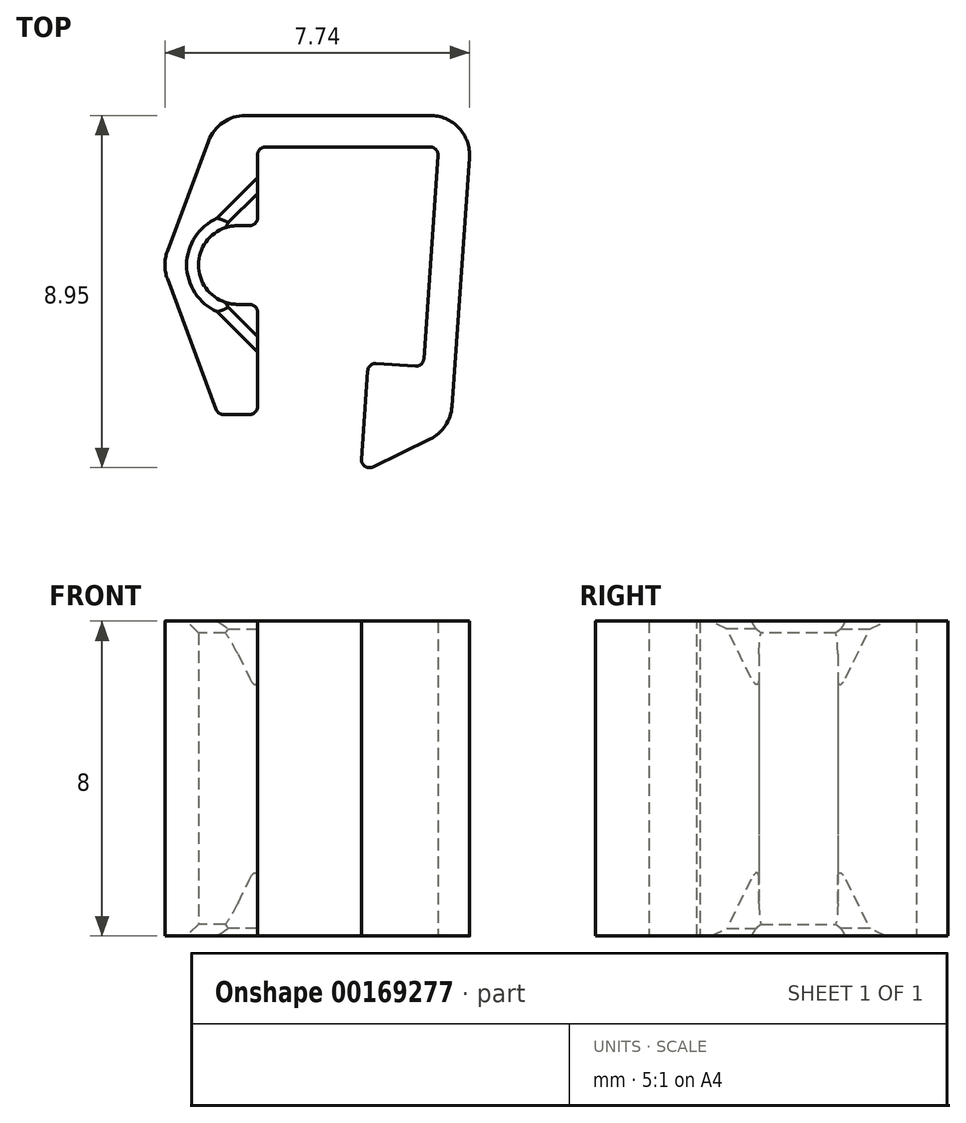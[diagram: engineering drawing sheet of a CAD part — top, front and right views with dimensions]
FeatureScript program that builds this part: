
annotation { "Feature Type Name" : "Feature", "Feature Type Description" : "" }
export const myFeature = defineFeature(function(context is Context, id is Id, definition is map)
    precondition{}
    {
        {
            var Q0;
            Q0=qCreatedBy(makeId("Top.planeOp"),FACE);
            var sketch = newSketch(context, id + "F0", { "sketchPlane" : qUnion([Q0])});
            skLineSegment(sketch, "E0", {"start": v(0, 0) * mm, "end": v(-0.4, -5.59) * mm});
            skLineSegment(sketch, "E1", {"start": v(-0.4, -5.59) * mm, "end": v(-1.79, -5.49) * mm});
            skLineSegment(sketch, "E2", {"start": v(-1.79, -5.49) * mm, "end": v(-1.98, -8.28) * mm});
            skLineSegment(sketch, "E3", {"start": v(-1.98, -8.28) * mm, "end": v(0.3, -7.17) * mm});
            skLineSegment(sketch, "E4", {"start": v(0.3, -7.17) * mm, "end": v(0.86, 0.8) * mm});
            skLineSegment(sketch, "E5", {"start": v(0.86, 0.8) * mm, "end": v(-5.6, 0.8) * mm});
            skLineSegment(sketch, "E6", {"start": v(-5.1, -4) * mm, "end": v(-4.6, -4) * mm});
            skLineSegment(sketch, "E7", {"start": v(-4.6, -4) * mm, "end": v(-4.6, -6.8) * mm});
            skLineSegment(sketch, "E8", {"start": v(-7.02, -3) * mm, "end": v(-5.6, -6.8) * mm});
            skLineSegment(sketch, "E9", {"start": v(-5.6, -6.8) * mm, "end": v(-4.6, -6.8) * mm});
            skLineSegment(sketch, "E10", {"start": v(-4.6, -2) * mm, "end": v(-5.1, -2) * mm});
            skLineSegment(sketch, "E11", {"start": v(0, 0) * mm, "end": v(-4.6, 0) * mm});
            skLineSegment(sketch, "E12", {"start": v(-4.6, 0) * mm, "end": v(-4.6, -2) * mm});
            skArc(sketch, "E13", {"start": v(-5.1, -2) * mm, "mid": v(-6.1, -3) * mm, "end": v(-5.1, -4) * mm});
            skLineSegment(sketch, "E14", {"start": v(-7.02, -3) * mm, "end": v(-5.6, 0.8) * mm});
            skLineSegment(sketch, "E15", {"start": v(-5.6, -6.8) * mm, "end": v(-5.6, 0.8) * mm, "construction": true});
            skLineSegment(sketch, "E16", {"start": v(-5.1, -3) * mm, "end": v(-6.04, -2.65) * mm, "construction": true});
            skLineSegment(sketch, "E17", {"start": v(-6.04, -2.65) * mm, "end": v(-6.79, -2.37) * mm, "construction": true});
            skLineSegment(sketch, "E18", {"start": v(0, 0) * mm, "end": v(0, 0.8) * mm, "construction": true});
            skLineSegment(sketch, "E19", {"start": v(0.8, -0.06) * mm, "end": v(0, 0) * mm, "construction": true});
            skSolve(sketch);
        }
        {
            var Q0;
            Q0 = qSketchRegion(id + "F0", true);
            extrude(context, id + "F1", {"entities" : qUnion([Q0]), "depth" : 4 * mm});
        }
        {
            var Q0;
            Q0=makeQuery(id+"F1.opExtrude","CAP_FACE",FACE,{"disambiguationData":[OSD([sQuery(id+"F0.wireOp",EDGE,"E0"),sQuery(id+"F0.wireOp",EDGE,"E1"),sQuery(id+"F0.wireOp",EDGE,"E2"),sQuery(id+"F0.wireOp",EDGE,"E3"),sQuery(id+"F0.wireOp",EDGE,"E4"),sQuery(id+"F0.wireOp",EDGE,"E5"),sQuery(id+"F0.wireOp",EDGE,"3qQk4eZ2-qFBK-7vCE-47k8-9gwiF50xY8QG"),sQuery(id+"F0.wireOp",EDGE,"FwfflrWr-MbD4-lGZ7-AJjG-6BkzjliF19me"),sQuery(id+"F0.wireOp",EDGE,"E6"),sQuery(id+"F0.wireOp",EDGE,"E7"),sQuery(id+"F0.wireOp",EDGE,"dEJFUDGW-VdPt-nXIw-TINV-OlQtnsbTHH9Y"),sQuery(id+"F0.wireOp",EDGE,"E8"),sQuery(id+"F0.wireOp",EDGE,"E9")])],"isStart":false});
            var sketch = newSketch(context, id + "F2", { "sketchPlane" : qUnion([Q0])});
            skLineSegment(sketch, "E20", {"start": v(-5.8, -3.7) * mm, "end": v(-4.6, -4.91) * mm});
            skLineSegment(sketch, "E21", {"start": v(-4.6, -4.91) * mm, "end": v(-4.6, -4) * mm});
            skLineSegment(sketch, "E22", {"start": v(-4.6, -4) * mm, "end": v(-5.8, -3.7) * mm});
            skLineSegment(sketch, "E23", {"start": v(-5.8, -2.3) * mm, "end": v(-4.6, -1.09) * mm});
            skLineSegment(sketch, "E24", {"start": v(-4.6, -1.09) * mm, "end": v(-4.6, -2) * mm});
            skLineSegment(sketch, "E25", {"start": v(-4.6, -2) * mm, "end": v(-5.8, -2.3) * mm});
            skSolve(sketch);
        }
        {
            var Q0;
            Q0 = qSketchRegion(id + "F2", true);
            extrude(context, id + "F3", {"entities" : qUnion([Q0]), "operationType" : NewBodyOperationType.REMOVE, "oppositeDirection" : true, "depth" : 2 * mm});
        }
        {
            var Q0;
            Q0=makeQuery(id+"F3.boolean.opBoolean","COPY",EDGE,{"derivedFrom":makeQuery(id+"F3.opExtrude","CAP_EDGE",EDGE,{"disambiguationData":[OSD([sQuery(id+"F2.wireOp",EDGE,"E20")])],"isStart":false})});
            chamfer(context, id + "F4", {"entities" : qUnion([Q0]), "chamferType" : ChamferType.TWO_OFFSETS, "width1" : .7 * mm, "oppositeDirection" : false, "width2" : 2 * mm, "tangentPropagation" : true});
        }
        {
            var Q0;
            Q0=makeQuery(id+"F3.boolean.opBoolean","COPY",EDGE,{"derivedFrom":makeQuery(id+"F3.opExtrude","CAP_EDGE",EDGE,{"disambiguationData":[OSD([sQuery(id+"F2.wireOp",EDGE,"E23")])],"isStart":false})});
            chamfer(context, id + "F5", {"entities" : qUnion([Q0]), "chamferType" : ChamferType.TWO_OFFSETS, "width1" : 2 * mm, "oppositeDirection" : false, "width2" : .7 * mm, "tangentPropagation" : true});
        }
        {
            var Q0;
            Q0=makeQuery(id+"F1.opExtrude","SWEPT_EDGE",EDGE,{"disambiguationData":[OSD([sQuery(id+"F0.wireOp",EDGE,"E0"),sQuery(id+"F0.wireOp",EDGE,"3qQk4eZ2-qFBK-7vCE-47k8-9gwiF50xY8QG")])]});
            var Q1;
            Q1=makeQuery(id+"F1.opExtrude","SWEPT_EDGE",EDGE,{"disambiguationData":[OSD([sQuery(id+"F0.wireOp",EDGE,"E0"),sQuery(id+"F0.wireOp",EDGE,"E1")])]});
            var Q2;
            Q2=makeQuery(id+"F1.opExtrude","SWEPT_EDGE",EDGE,{"disambiguationData":[OSD([sQuery(id+"F0.wireOp",EDGE,"E1"),sQuery(id+"F0.wireOp",EDGE,"E2")])]});
            var Q3;
            Q3=makeQuery(id+"F1.opExtrude","SWEPT_EDGE",EDGE,{"disambiguationData":[OSD([sQuery(id+"F0.wireOp",EDGE,"E2"),sQuery(id+"F0.wireOp",EDGE,"E3")])]});
            var Q4;
            Q4=makeQuery(id+"F1.opExtrude","SWEPT_EDGE",EDGE,{"disambiguationData":[OSD([sQuery(id+"F0.wireOp",EDGE,"E7"),sQuery(id+"F0.wireOp",EDGE,"E9")])]});
            var Q5;
            Q5=makeQuery(id+"F1.opExtrude","SWEPT_EDGE",EDGE,{"disambiguationData":[OSD([sQuery(id+"F0.wireOp",EDGE,"E6"),sQuery(id+"F0.wireOp",EDGE,"E7")])]});
            var Q6;
            Q6=makeQuery(id+"F1.opExtrude","SWEPT_EDGE",EDGE,{"disambiguationData":[OSD([sQuery(id+"F0.wireOp",EDGE,"E10"),sQuery(id+"F0.wireOp",EDGE,"E12")])]});
            var Q7;
            Q7=makeQuery(id+"F1.opExtrude","SWEPT_EDGE",EDGE,{"disambiguationData":[OSD([sQuery(id+"F0.wireOp",EDGE,"E8"),sQuery(id+"F0.wireOp",EDGE,"E9")])]});
            var Q8;
            Q8=makeQuery(id+"F1.opExtrude","SWEPT_EDGE",EDGE,{"disambiguationData":[OSD([sQuery(id+"F0.wireOp",EDGE,"E11"),sQuery(id+"F0.wireOp",EDGE,"E12")])]});
            fillet(context, id + "F6", {"entities" : qUnion([Q0, Q1, Q2, Q3, Q4, Q5, Q6, Q7, Q8]), "radius" : .2 * mm, "tangentPropagation" : true, "allowEdgeOverflow" : false});
        }
        {
            var Q0;
            Q0=makeQuery(id+"F1.opExtrude","SWEPT_EDGE",EDGE,{"disambiguationData":[OSD([sQuery(id+"F0.wireOp",EDGE,"E4"),sQuery(id+"F0.wireOp",EDGE,"E5")])]});
            var Q1;
            Q1=makeQuery(id+"F1.opExtrude","SWEPT_EDGE",EDGE,{"disambiguationData":[OSD([sQuery(id+"F0.wireOp",EDGE,"E3"),sQuery(id+"F0.wireOp",EDGE,"E4")])]});
            var Q2;
            Q2=makeQuery(id+"F1.opExtrude","SWEPT_EDGE",EDGE,{"disambiguationData":[OSD([sQuery(id+"F0.wireOp",EDGE,"E8"),sQuery(id+"F0.wireOp",EDGE,"E9")])]});
            var Q3;
            Q3=makeQuery(id+"F1.opExtrude","SWEPT_EDGE",EDGE,{"disambiguationData":[OSD([sQuery(id+"F0.wireOp",EDGE,"E8"),sQuery(id+"F0.wireOp",EDGE,"E14")])]});
            var Q4;
            Q4=makeQuery(id+"F1.opExtrude","SWEPT_EDGE",EDGE,{"disambiguationData":[OSD([sQuery(id+"F0.wireOp",EDGE,"E5"),sQuery(id+"F0.wireOp",EDGE,"E14")])]});
            fillet(context, id + "F7", {"entities" : qUnion([Q0, Q1, Q2, Q3, Q4]), "radius" : 1 * mm, "tangentPropagation" : true, "allowEdgeOverflow" : false});
        }
        {
            var Q0;
            Q0=makeQuery(id+"F1.opExtrude","SWEPT_BODY",BODY,{"disambiguationData":[OSD([sQuery(id+"F0.wireOp",EDGE,"E0"),sQuery(id+"F0.wireOp",EDGE,"E1"),sQuery(id+"F0.wireOp",EDGE,"E2"),sQuery(id+"F0.wireOp",EDGE,"E3"),sQuery(id+"F0.wireOp",EDGE,"E4"),sQuery(id+"F0.wireOp",EDGE,"E5"),sQuery(id+"F0.wireOp",EDGE,"3qQk4eZ2-qFBK-7vCE-47k8-9gwiF50xY8QG"),sQuery(id+"F0.wireOp",EDGE,"FwfflrWr-MbD4-lGZ7-AJjG-6BkzjliF19me"),sQuery(id+"F0.wireOp",EDGE,"E6"),sQuery(id+"F0.wireOp",EDGE,"E7"),sQuery(id+"F0.wireOp",EDGE,"dEJFUDGW-VdPt-nXIw-TINV-OlQtnsbTHH9Y"),sQuery(id+"F0.wireOp",EDGE,"E8"),sQuery(id+"F0.wireOp",EDGE,"E9")])]});
            var Q1;
            Q1=makeQuery(id+"F1.opExtrude","CAP_FACE",FACE,{"disambiguationData":[OSD([sQuery(id+"F0.wireOp",EDGE,"E0"),sQuery(id+"F0.wireOp",EDGE,"E1"),sQuery(id+"F0.wireOp",EDGE,"E2"),sQuery(id+"F0.wireOp",EDGE,"E3"),sQuery(id+"F0.wireOp",EDGE,"E4"),sQuery(id+"F0.wireOp",EDGE,"E5"),sQuery(id+"F0.wireOp",EDGE,"3qQk4eZ2-qFBK-7vCE-47k8-9gwiF50xY8QG"),sQuery(id+"F0.wireOp",EDGE,"FwfflrWr-MbD4-lGZ7-AJjG-6BkzjliF19me"),sQuery(id+"F0.wireOp",EDGE,"E6"),sQuery(id+"F0.wireOp",EDGE,"E7"),sQuery(id+"F0.wireOp",EDGE,"dEJFUDGW-VdPt-nXIw-TINV-OlQtnsbTHH9Y"),sQuery(id+"F0.wireOp",EDGE,"E8"),sQuery(id+"F0.wireOp",EDGE,"E9")])],"isStart":true});
            mirror(context, id + "F8", {"operationType" : NewBodyOperationType.ADD, "entities" : qUnion([Q0]), "mirrorPlane" : qUnion([Q1])});
        }
        {
            var Q0;
            Q0=makeQuery(id+"F1.opExtrude","CAP_EDGE",EDGE,{"disambiguationData":[OSD([sQuery(id+"F0.wireOp",EDGE,"E13")])],"isStart":false});
            var Q1;
            Q1=makeQuery(id+"F5.opChamfer","BLEND_EDGE",EDGE,{"blendedFrom":[makeQuery(id+"F3.boolean.opBoolean","COPY",EDGE,{"derivedFrom":makeQuery(id+"F3.opExtrude","CAP_EDGE",EDGE,{"disambiguationData":[OSD([sQuery(id+"F2.wireOp",EDGE,"E23")])],"isStart":false})}),makeQuery(id+"F1.opExtrude","CAP_FACE",FACE,{"disambiguationData":[OSD([sQuery(id+"F0.wireOp",EDGE,"E0"),sQuery(id+"F0.wireOp",EDGE,"E1"),sQuery(id+"F0.wireOp",EDGE,"E2"),sQuery(id+"F0.wireOp",EDGE,"E3"),sQuery(id+"F0.wireOp",EDGE,"E4"),sQuery(id+"F0.wireOp",EDGE,"E5"),sQuery(id+"F0.wireOp",EDGE,"E6"),sQuery(id+"F0.wireOp",EDGE,"E7"),sQuery(id+"F0.wireOp",EDGE,"E8"),sQuery(id+"F0.wireOp",EDGE,"E9"),sQuery(id+"F0.wireOp",EDGE,"E10"),sQuery(id+"F0.wireOp",EDGE,"E11"),sQuery(id+"F0.wireOp",EDGE,"E12"),sQuery(id+"F0.wireOp",EDGE,"E13"),sQuery(id+"F0.wireOp",EDGE,"E14")])],"isStart":false})],"blendedInto":[makeQuery(id+"F1.opExtrude","CAP_FACE",FACE,{"disambiguationData":[OSD([sQuery(id+"F0.wireOp",EDGE,"E0"),sQuery(id+"F0.wireOp",EDGE,"E1"),sQuery(id+"F0.wireOp",EDGE,"E2"),sQuery(id+"F0.wireOp",EDGE,"E3"),sQuery(id+"F0.wireOp",EDGE,"E4"),sQuery(id+"F0.wireOp",EDGE,"E5"),sQuery(id+"F0.wireOp",EDGE,"E6"),sQuery(id+"F0.wireOp",EDGE,"E7"),sQuery(id+"F0.wireOp",EDGE,"E8"),sQuery(id+"F0.wireOp",EDGE,"E9"),sQuery(id+"F0.wireOp",EDGE,"E10"),sQuery(id+"F0.wireOp",EDGE,"E11"),sQuery(id+"F0.wireOp",EDGE,"E12"),sQuery(id+"F0.wireOp",EDGE,"E13"),sQuery(id+"F0.wireOp",EDGE,"E14")])],"isStart":false})]});
            var Q2;
            Q2=makeQuery(id+"F4.opChamfer","BLEND_EDGE",EDGE,{"blendedFrom":[makeQuery(id+"F3.boolean.opBoolean","COPY",EDGE,{"derivedFrom":makeQuery(id+"F3.opExtrude","CAP_EDGE",EDGE,{"disambiguationData":[OSD([sQuery(id+"F2.wireOp",EDGE,"E20")])],"isStart":false})}),makeQuery(id+"F1.opExtrude","CAP_FACE",FACE,{"disambiguationData":[OSD([sQuery(id+"F0.wireOp",EDGE,"E0"),sQuery(id+"F0.wireOp",EDGE,"E1"),sQuery(id+"F0.wireOp",EDGE,"E2"),sQuery(id+"F0.wireOp",EDGE,"E3"),sQuery(id+"F0.wireOp",EDGE,"E4"),sQuery(id+"F0.wireOp",EDGE,"E5"),sQuery(id+"F0.wireOp",EDGE,"E6"),sQuery(id+"F0.wireOp",EDGE,"E7"),sQuery(id+"F0.wireOp",EDGE,"E8"),sQuery(id+"F0.wireOp",EDGE,"E9"),sQuery(id+"F0.wireOp",EDGE,"E10"),sQuery(id+"F0.wireOp",EDGE,"E11"),sQuery(id+"F0.wireOp",EDGE,"E12"),sQuery(id+"F0.wireOp",EDGE,"E13"),sQuery(id+"F0.wireOp",EDGE,"E14")])],"isStart":false})],"blendedInto":[makeQuery(id+"F1.opExtrude","CAP_FACE",FACE,{"disambiguationData":[OSD([sQuery(id+"F0.wireOp",EDGE,"E0"),sQuery(id+"F0.wireOp",EDGE,"E1"),sQuery(id+"F0.wireOp",EDGE,"E2"),sQuery(id+"F0.wireOp",EDGE,"E3"),sQuery(id+"F0.wireOp",EDGE,"E4"),sQuery(id+"F0.wireOp",EDGE,"E5"),sQuery(id+"F0.wireOp",EDGE,"E6"),sQuery(id+"F0.wireOp",EDGE,"E7"),sQuery(id+"F0.wireOp",EDGE,"E8"),sQuery(id+"F0.wireOp",EDGE,"E9"),sQuery(id+"F0.wireOp",EDGE,"E10"),sQuery(id+"F0.wireOp",EDGE,"E11"),sQuery(id+"F0.wireOp",EDGE,"E12"),sQuery(id+"F0.wireOp",EDGE,"E13"),sQuery(id+"F0.wireOp",EDGE,"E14")])],"isStart":false})]});
            var Q3;
            Q3=makeQuery(id+"F8.opPattern","COPY",EDGE,{"derivedFrom":makeQuery(id+"F1.opExtrude","CAP_EDGE",EDGE,{"disambiguationData":[OSD([sQuery(id+"F0.wireOp",EDGE,"E13")])],"isStart":false}),"instanceName":"1"});
            var Q4;
            Q4=makeQuery(id+"F8.opPattern","COPY",EDGE,{"derivedFrom":makeQuery(id+"F5.opChamfer","BLEND_EDGE",EDGE,{"blendedFrom":[makeQuery(id+"F3.boolean.opBoolean","COPY",EDGE,{"derivedFrom":makeQuery(id+"F3.opExtrude","CAP_EDGE",EDGE,{"disambiguationData":[OSD([sQuery(id+"F2.wireOp",EDGE,"E23")])],"isStart":false})}),makeQuery(id+"F1.opExtrude","CAP_FACE",FACE,{"disambiguationData":[OSD([sQuery(id+"F0.wireOp",EDGE,"E0"),sQuery(id+"F0.wireOp",EDGE,"E1"),sQuery(id+"F0.wireOp",EDGE,"E2"),sQuery(id+"F0.wireOp",EDGE,"E3"),sQuery(id+"F0.wireOp",EDGE,"E4"),sQuery(id+"F0.wireOp",EDGE,"E5"),sQuery(id+"F0.wireOp",EDGE,"E6"),sQuery(id+"F0.wireOp",EDGE,"E7"),sQuery(id+"F0.wireOp",EDGE,"E8"),sQuery(id+"F0.wireOp",EDGE,"E9"),sQuery(id+"F0.wireOp",EDGE,"E10"),sQuery(id+"F0.wireOp",EDGE,"E11"),sQuery(id+"F0.wireOp",EDGE,"E12"),sQuery(id+"F0.wireOp",EDGE,"E13"),sQuery(id+"F0.wireOp",EDGE,"E14")])],"isStart":false})],"blendedInto":[makeQuery(id+"F1.opExtrude","CAP_FACE",FACE,{"disambiguationData":[OSD([sQuery(id+"F0.wireOp",EDGE,"E0"),sQuery(id+"F0.wireOp",EDGE,"E1"),sQuery(id+"F0.wireOp",EDGE,"E2"),sQuery(id+"F0.wireOp",EDGE,"E3"),sQuery(id+"F0.wireOp",EDGE,"E4"),sQuery(id+"F0.wireOp",EDGE,"E5"),sQuery(id+"F0.wireOp",EDGE,"E6"),sQuery(id+"F0.wireOp",EDGE,"E7"),sQuery(id+"F0.wireOp",EDGE,"E8"),sQuery(id+"F0.wireOp",EDGE,"E9"),sQuery(id+"F0.wireOp",EDGE,"E10"),sQuery(id+"F0.wireOp",EDGE,"E11"),sQuery(id+"F0.wireOp",EDGE,"E12"),sQuery(id+"F0.wireOp",EDGE,"E13"),sQuery(id+"F0.wireOp",EDGE,"E14")])],"isStart":false})]}),"instanceName":"1"});
            var Q5;
            Q5=makeQuery(id+"F8.opPattern","COPY",EDGE,{"derivedFrom":makeQuery(id+"F4.opChamfer","BLEND_EDGE",EDGE,{"blendedFrom":[makeQuery(id+"F3.boolean.opBoolean","COPY",EDGE,{"derivedFrom":makeQuery(id+"F3.opExtrude","CAP_EDGE",EDGE,{"disambiguationData":[OSD([sQuery(id+"F2.wireOp",EDGE,"E20")])],"isStart":false})}),makeQuery(id+"F1.opExtrude","CAP_FACE",FACE,{"disambiguationData":[OSD([sQuery(id+"F0.wireOp",EDGE,"E0"),sQuery(id+"F0.wireOp",EDGE,"E1"),sQuery(id+"F0.wireOp",EDGE,"E2"),sQuery(id+"F0.wireOp",EDGE,"E3"),sQuery(id+"F0.wireOp",EDGE,"E4"),sQuery(id+"F0.wireOp",EDGE,"E5"),sQuery(id+"F0.wireOp",EDGE,"E6"),sQuery(id+"F0.wireOp",EDGE,"E7"),sQuery(id+"F0.wireOp",EDGE,"E8"),sQuery(id+"F0.wireOp",EDGE,"E9"),sQuery(id+"F0.wireOp",EDGE,"E10"),sQuery(id+"F0.wireOp",EDGE,"E11"),sQuery(id+"F0.wireOp",EDGE,"E12"),sQuery(id+"F0.wireOp",EDGE,"E13"),sQuery(id+"F0.wireOp",EDGE,"E14")])],"isStart":false})],"blendedInto":[makeQuery(id+"F1.opExtrude","CAP_FACE",FACE,{"disambiguationData":[OSD([sQuery(id+"F0.wireOp",EDGE,"E0"),sQuery(id+"F0.wireOp",EDGE,"E1"),sQuery(id+"F0.wireOp",EDGE,"E2"),sQuery(id+"F0.wireOp",EDGE,"E3"),sQuery(id+"F0.wireOp",EDGE,"E4"),sQuery(id+"F0.wireOp",EDGE,"E5"),sQuery(id+"F0.wireOp",EDGE,"E6"),sQuery(id+"F0.wireOp",EDGE,"E7"),sQuery(id+"F0.wireOp",EDGE,"E8"),sQuery(id+"F0.wireOp",EDGE,"E9"),sQuery(id+"F0.wireOp",EDGE,"E10"),sQuery(id+"F0.wireOp",EDGE,"E11"),sQuery(id+"F0.wireOp",EDGE,"E12"),sQuery(id+"F0.wireOp",EDGE,"E13"),sQuery(id+"F0.wireOp",EDGE,"E14")])],"isStart":false})]}),"instanceName":"1"});
            chamfer(context, id + "F9", {"entities" : qUnion([Q0, Q1, Q2, Q3, Q4, Q5]), "chamferType" : ChamferType.OFFSET_ANGLE, "width" : .3 * mm, "oppositeDirection" : false, "angle" : 45 * degree, "tangentPropagation" : true});
        }
    });
